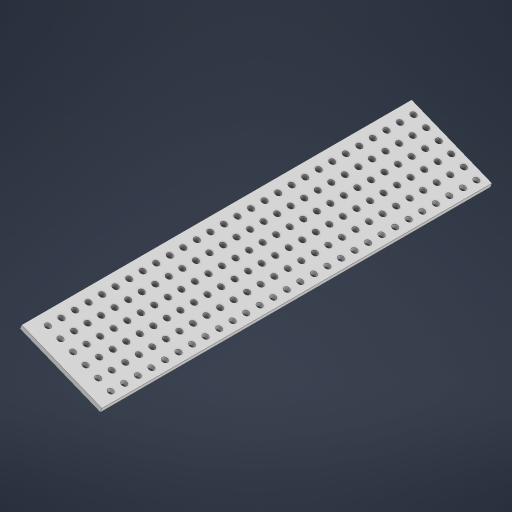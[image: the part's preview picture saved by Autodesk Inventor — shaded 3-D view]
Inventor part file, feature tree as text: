
AUTODESK INVENTOR PART (.ipt)
format: ipt  version: 2023 (Build 270158000, 158)  size: 331,776 bytes
history: native  units: mm
features: other x3, extrude x2, sketch x2, reference x2, pattern_linear x1, projected_geometry x1
ambient origin geometry x8: Origin, YZ Plane, XZ Plane, XY Plane, X Axis, Y Axis, Z Axis, Center Point
bodies: Solid1 (feature_tree)
feature tree (11):
  extrude  "Extrusion1"  Depth=288.0mm
  extrude  "Extrusion2"  Depth=63.9mm
  pattern_linear  "Rectangular Pattern1"  Spacing1=288.0mm  [1 undecoded]
  sketch  "Sketch1"  dims[d0=288.0mm d1=0.0mm d2=4.0mm]
  reference  "Reference1"
  reference  "Reference2"
  sketch  "Sketch2"  dims[d3=6.0mm d4=6.0mm d5=288.0mm d6=0.0mm d7=280.0mm d9=10.0mm d10=60.0mm d12=10.0mm d13=63.9mm]
  projected_geometry  "Projected Loop1"
  parser-record x1  (decoder bookkeeping rows leaked as tree rows — omitted from the tree; the rows remain in map.json)
  other  "assembly.iam"
  other  "deckel:1"
note: 1 required parameter value undecoded (feature->parameter linkage not recoverable at this tier; creation-order binding heuristic only, values carry confidence <= 0.55)
note: 1 file-system path scrubbed to <path> (originals preserved in map.json)
